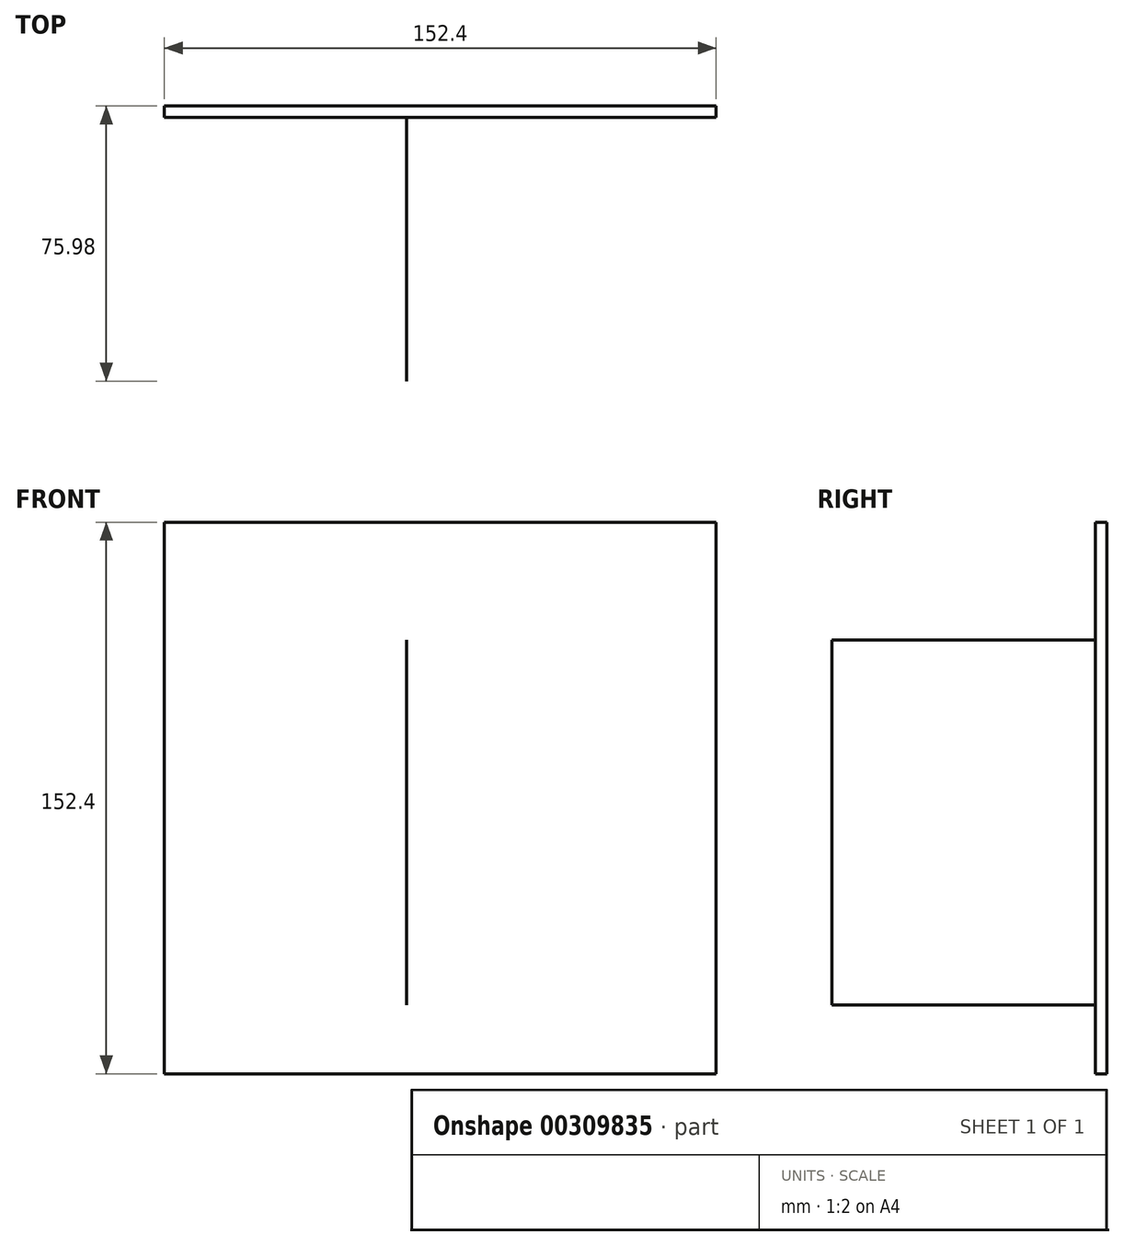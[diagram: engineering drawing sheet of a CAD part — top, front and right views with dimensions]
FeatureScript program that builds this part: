
annotation { "Feature Type Name" : "Feature", "Feature Type Description" : "" }
export const myFeature = defineFeature(function(context is Context, id is Id, definition is map)
    precondition{}
    {
        {
            var Q0;
            Q0=qCreatedBy(makeId("Front.planeOp"),FACE);
            var sketch = newSketch(context, id + "F0", { "sketchPlane" : qUnion([Q0])});
            skLineSegment(sketch, "E0.bottom", {"start": v(-66.96, 82.16) * mm, "end": v(85.44, 82.16) * mm});
            skLineSegment(sketch, "E0.top", {"start": v(-66.96, -70.24) * mm, "end": v(85.44, -70.24) * mm});
            skLineSegment(sketch, "E0.left", {"start": v(-66.96, 82.16) * mm, "end": v(-66.96, -70.24) * mm});
            skLineSegment(sketch, "E0.right", {"start": v(85.44, 82.16) * mm, "end": v(85.44, -70.24) * mm});
            skSolve(sketch);
        }
        {
            var Q0;
            Q0 = qSketchRegion(id + "F0", true);
            var Q1;
            Q1 = qSketchRegion(id + "FAaD9UyIaGZgiYP_1", true);
            extrude(context, id + "F1", {"entities" : qUnion([Q0, Q1]), "depth" : 3.17 * mm});
        }
        {
            var Q0;
            Q0=qCreatedBy(makeId("Right.planeOp"),FACE);
            var sketch = newSketch(context, id + "F2", { "sketchPlane" : qUnion([Q0])});
            skLineSegment(sketch, "E1", {"start": v(0, 0) * mm, "end": v(-73.02, 0) * mm});
            skLineSegment(sketch, "E2", {"start": v(0, 49.62) * mm, "end": v(-75.98, 49.62) * mm});
            skLineSegment(sketch, "E3", {"start": v(0, -51.23) * mm, "end": v(-75.98, -51.23) * mm});
            skLineSegment(sketch, "E4", {"start": v(-75.98, -51.23) * mm, "end": v(-75.98, 49.62) * mm});
            skLineSegment(sketch, "E5", {"start": v(0, -51.23) * mm, "end": v(0, 49.62) * mm});
            skSolve(sketch);
        }
        {
            var Q0;
            Q0 = qSketchRegion(id + "F2", true);
            extrude(context, id + "F3", {"entities" : qUnion([Q0]), "operationType" : NewBodyOperationType.ADD, "depth" : 1 / 101.6 * mm});
        }
    });
